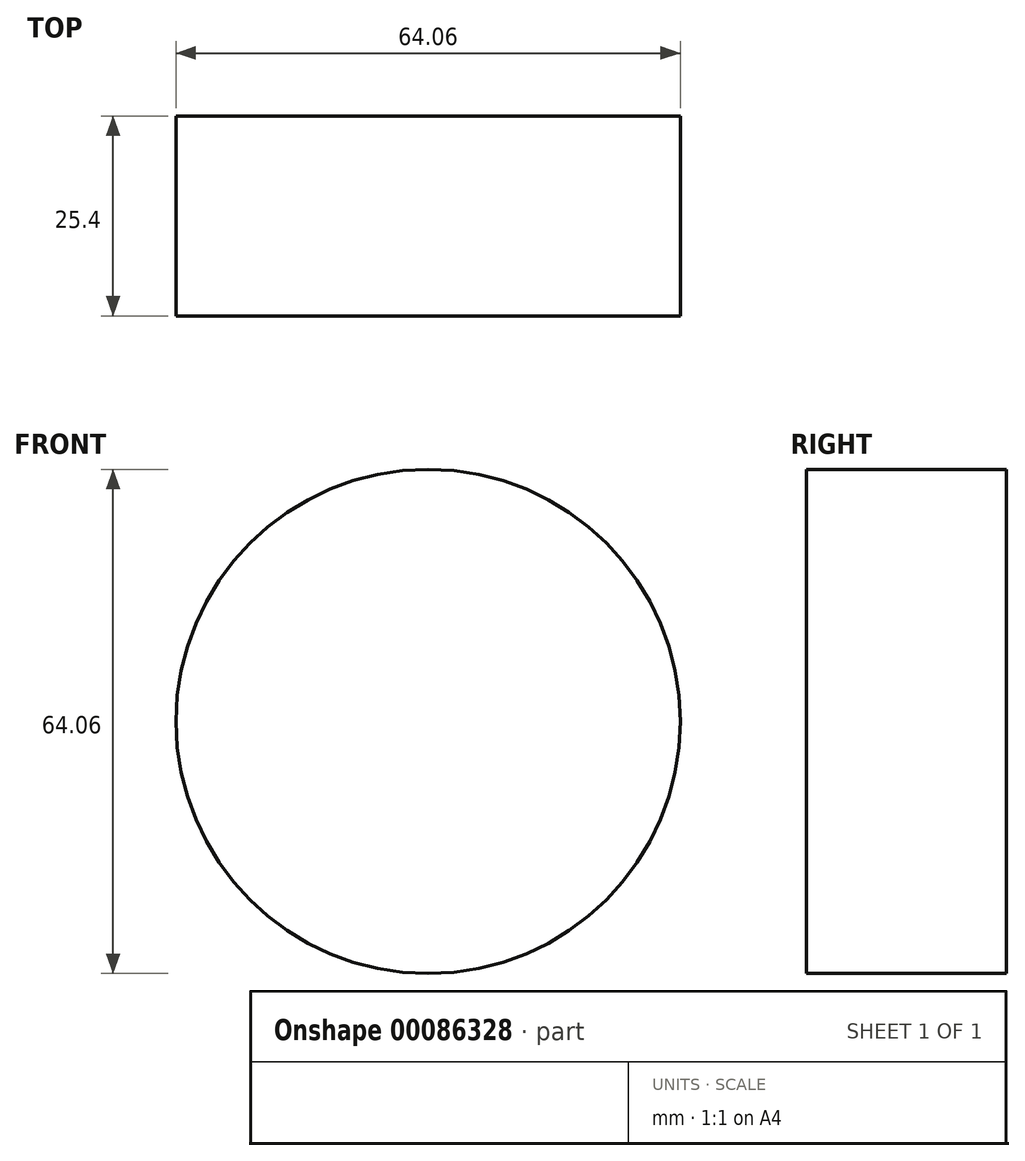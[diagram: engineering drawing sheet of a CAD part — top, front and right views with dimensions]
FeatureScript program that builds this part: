
annotation { "Feature Type Name" : "Feature", "Feature Type Description" : "" }
export const myFeature = defineFeature(function(context is Context, id is Id, definition is map)
    precondition{}
    {
        {
            var Q0;
            Q0=qCreatedBy(makeId("Front.planeOp"),FACE);
            var sketch = newSketch(context, id + "F0", { "sketchPlane" : qUnion([Q0])});
            skCircle(sketch, "E0", {"center": v(0, 0) * mm, "radius": 32.03 * mm});
            skSolve(sketch);
        }
        {
            var Q0;
            Q0 = qSketchRegion(id + "F0", true);
            extrude(context, id + "F1", {"entities" : qUnion([Q0]), "depth" : 25.4 * mm});
        }
    });
